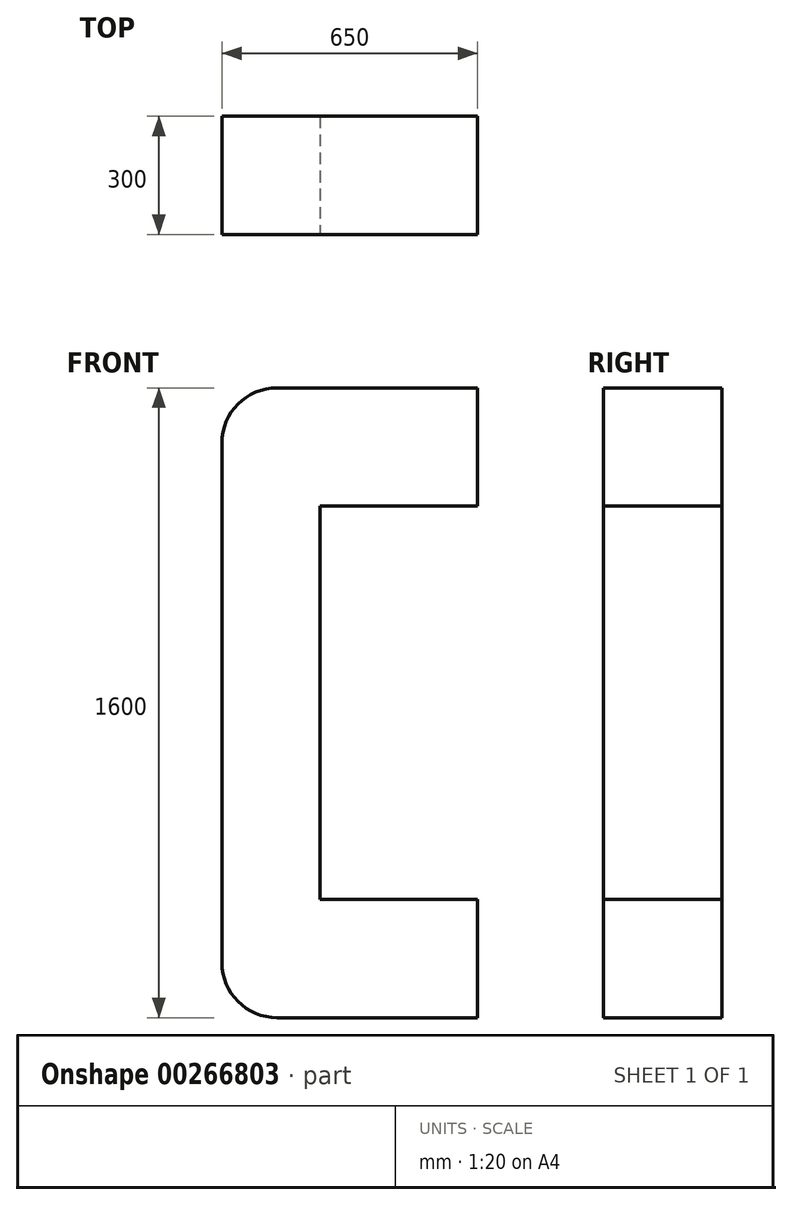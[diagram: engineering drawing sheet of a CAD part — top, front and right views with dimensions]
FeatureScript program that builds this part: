
annotation { "Feature Type Name" : "Feature", "Feature Type Description" : "" }
export const myFeature = defineFeature(function(context is Context, id is Id, definition is map)
    precondition{}
    {
        {
            var Q0;
            Q0=qCreatedBy(makeId("Front.planeOp"),FACE);
            var sketch = newSketch(context, id + "F0", { "sketchPlane" : qUnion([Q0])});
            skLineSegment(sketch, "E0", {"start": v(-356.98, 749.15) * mm, "end": v(-356.98, -570.85) * mm});
            skLineSegment(sketch, "E1", {"start": v(-216.98, 889.15) * mm, "end": v(293.02, 889.15) * mm});
            skLineSegment(sketch, "E2", {"start": v(-216.98, -710.85) * mm, "end": v(293.02, -710.85) * mm});
            skLineSegment(sketch, "E3", {"start": v(293.02, 889.15) * mm, "end": v(293.02, 589.15) * mm});
            skLineSegment(sketch, "E4", {"start": v(293.02, 589.15) * mm, "end": v(-106.98, 589.15) * mm});
            skLineSegment(sketch, "E5", {"start": v(-106.98, 589.15) * mm, "end": v(-106.98, -410.85) * mm});
            skLineSegment(sketch, "E6", {"start": v(-106.98, -410.85) * mm, "end": v(293.02, -410.85) * mm});
            skLineSegment(sketch, "E7", {"start": v(293.02, -410.85) * mm, "end": v(293.02, -710.85) * mm});
            skPoint(sketch, "E8.visualSharp", {"position": v(-356.98, 889.15) * mm});
            skArc(sketch, "E8.filletArc", {"start": v(-216.98, 889.15) * mm, "mid": v(-315.98, 848.15) * mm, "end": v(-356.98, 749.15) * mm});
            skPoint(sketch, "E9.visualSharp", {"position": v(-356.98, -710.85) * mm});
            skArc(sketch, "E9.filletArc", {"start": v(-356.98, -570.85) * mm, "mid": v(-315.98, -669.84) * mm, "end": v(-216.98, -710.85) * mm});
            skSolve(sketch);
        }
        {
            var Q0;
            Q0=makeQuery(id+"F0.imprint","IMPRINT",FACE,{"disambiguationData":[TD([[makeQuery(id+"F0.imprint","IMPRINT",EDGE,{"derivedFrom":sQuery(id+"F0.wireOp",EDGE,"E0")}),1.0]])]});
            extrude(context, id + "F1", {"entities" : qUnion([Q0]), "oppositeDirection" : true, "depth" : 300 * mm});
        }
    });
